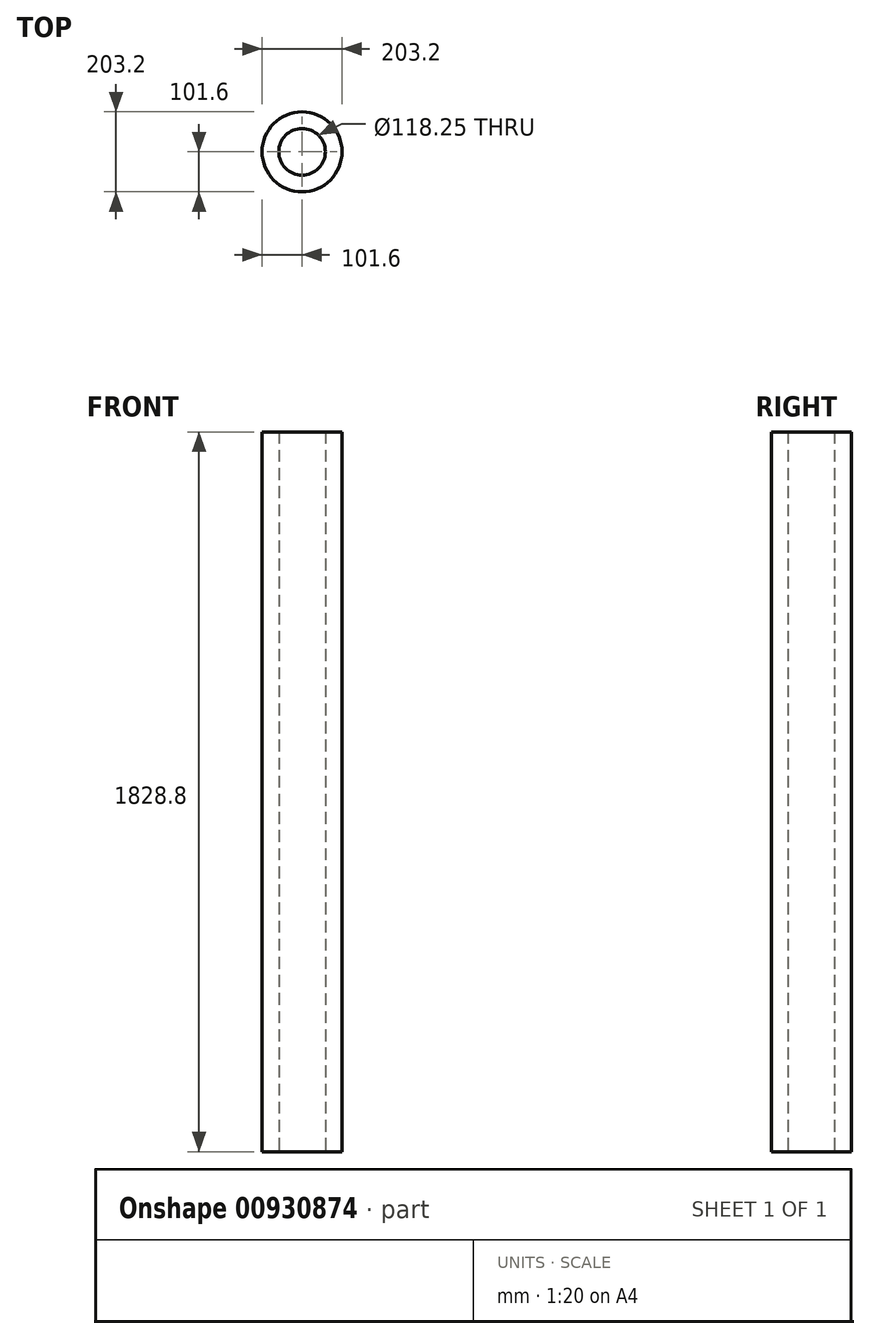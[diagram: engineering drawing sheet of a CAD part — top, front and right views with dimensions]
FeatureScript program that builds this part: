
annotation { "Feature Type Name" : "Feature", "Feature Type Description" : "" }
export const myFeature = defineFeature(function(context is Context, id is Id, definition is map)
    precondition{}
    {
        {
            var Q0;
            Q0=qCreatedBy(makeId("Top.planeOp"),FACE);
            var sketch = newSketch(context, id + "F0", { "sketchPlane" : qUnion([Q0])});
            skCircle(sketch, "E0", {"center": v(0, 0) * mm, "radius": 101.6 * mm});
            skCircle(sketch, "E1", {"center": v(0, 0) * mm, "radius": 59.13 * mm});
            skSolve(sketch);
        }
        {
            var Q0;
            Q0=makeQuery(id+"F0.imprint","IMPRINT",FACE,{"disambiguationData":[TD([[makeQuery(id+"F0.imprint","IMPRINT",EDGE,{"derivedFrom":sQuery(id+"F0.wireOp",EDGE,"E0")}),1.0]])]});
            extrude(context, id + "F1", {"entities" : qUnion([Q0]), "depth" : 1828.8 * mm, "offsetDistance" : 25.4 * mm});
        }
    });
